# Revit family: CCIRC Emergency Circular Lighting_Non-Hosted_R19
name_source: partatom
category: Lighting Fixtures
units: mm (PartAtom-declared; Revit-internal decimal feet)

## family parameters
Always vertical = Yes
Cut with Voids When Loaded = No
Light Source = Yes
OmniClass Number = 23.80.70.00
OmniClass Title = Lighting
Part Type = Normal
Room Calculation Point = No
Round Connector Dimension = Use Diameter
Shared = No
Work Plane-Based = No

## types (7) — shared parameters
Applicable Standards = BS EN 60598.2.22, BS 5266
Battery Type = Lithium Iron Phosphate (LiFePO4)
Charging Method = Intelligent Current Limited Constant Voltage
Color Filter = 16777215
Construction = Polycarbonate
Diffuser = Polycarbonate Diffuser
Dimensions (L x W x H) = 327mm (Diameter) x 100mm (Height)
Dimming Lamp Color Temperature Shift = <None>
Emit Shape Visible in Rendering = No
IP Rating = IP54
Lamp = LED module, 4,000K natural white, 50,000h life, Ra>80
Manufacturer = Clevertronics
Mounting = Surface Mount
Operating Mode = Sustained
Operating Temperature = 1˚C to 40˚C
Photometric Web File = 6002_CCIRC-HV(S4)_EM220mA_23082021-02_IES2002.IES
Tilt Angle = 90.00°
Weight = 1.8 kg
zero-valued in all types: Default Elevation

## per-type parameters (varying)
| type | AS2293 Classification | Description | MIC Number | Operating Voltage | Power Consumption (Lamp ON Max Charge) | Power Consumption (Lamp ON Standby Charge) | Power Consumption (Lamp Off Standby) | Power Factor | Replacement Battery | Replacement Driver | Replacement Emergency Driver | Replacement Item | Replacement lamp | Sensor | Testing System | Total Lumen Output | Type Comments |
| CCIRC-ZW |  | CLP Premium Circular LED Emergency Luminaire, Trim colour white | UKC02110010001 | 220-240V AC; 50Hz | 16.5 Watts | 13W | 1.3W |  | 1550230 BATT:LP 3.2V 6400mAh.200mm lead.Brkt. | 1330091 LED Driver - 20w Stallion, 380mA | UKM02170190001 CLIFE-CKIT-ZW-IC1-650, Lifelight, Control Only, LP, ZW, 650mA, No Plug | 8001450 PCA:Powerline Node ZW, #CT10310-A6 | 8002801 PCA: CLE 220mm 2500lm 840 ADV4 EM SO |  | Zoneworks computerised testing | 1300lm @104lm/W |  |
| CCIRC | C0=D40 C90=D40 | LP Premium Circular LED Emergency Luminaire, Trim colour white, 
Enabled with Clevertest Plus
LP Premium Circular LED Emergency Luminaire, Trim colour white, 
Enabled with Clevertest Plus
LP Premium Circular LED Emergency Luminaire, Trim colour White, Enabled with Clevertest Plus | AUC02310010001 | 220-240V AC; 50Hz | 15 W | 13 W | 1.0 W | 0.93 | 1550010 | 1330091 | AUM02370470001
CLIFE-CKIT-NP-220
AUM02370470001
CLIFE-CKIT-NP-220
AUM02370470001
CLIFE-CKIT-NP-220
AUM02370470001
CLIFE-CKIT-NP-220
AUM02370470001 - CLIFE-CKIT-NP-220 |  | 8002801 |  | Clevertest Plus Enabled (Not activated by default) | 1300lm @104lm/W |  |
| CCIRC-HV | C0=D40 C90=D40 | LP Premium Circular LED Emergency Luminaire, Trim colour white | AUC02810020001 | 220-240V AC; 50Hz | 16 W | 13 W | 1.3 W | 0.93 | 1550010 | 1330091 | AUM02870500001 CLIFE-CKIT-HV-NP-220 | 8003191 | 8011800 |  | Zoneworks XT HIVE (RF) | 1460lm @118lm/W | Circular, LED, LP, Hive |
| CCIRC-MS-HL | C0=D25 C90=D25 | LP Premium Circular LED Emergency Luminaire with Microwave Sensor Control 
of the Lamps (Hi/Lo function), Trim colour white, Enabled with Clevertest Plus
LP Premium Circular LED Emergency Luminaire with Microwave Sensor Control 
of the Lamps (Hi/Lo function), Trim colour white, Enabled with Clevertest Plus
LP Premium Circular LED Emergency Luminaire with Microwave Sensor Control 
of the Lamps (Hi/Lo function), Trim colour white, Enabled with Clevertest Plus
LP Premium Circular LED Emergency Luminaire with Microwave Sensor Control 
of the Lamps (Hi/Lo function), Trim colour white, Enabled with Clevertest Plus
LP Premium Circular LED Emergency Luminaire with Microwave Sensor Control 
of the Lamps (Hi/Lo function), Trim colour white, Enabled with Clevertest Plus
LP Premium Circular LED Emergency Luminaire with Microwave Sensor Control 
of the Lamps (Hi/Lo function), Trim colour white, Enabled with Clevertest Plus
LP Premium Circular LED Emergency Luminaire with Microwave Sensor Control 
of the Lamps (Hi/Lo function), Trim colour white, Enabled with Clevertest Plus
LP Premium Circular LED Emergency Luminaire with Microwave Sensor Control 
of the Lamps (Hi/Lo function), Trim colour white, Enabled with Clevertest Plus
LP Premium Circular LED Emergency Luminaire with Microwave Sensor Control 
of the Lamps (Hi/Lo function), Trim colour white, Enabled with Clevertest Plus
LP Premium Circular LED Emergency Luminaire with Microwave Sensor Control of the Lamps (Hi/Lo function), Trim colour white, Enabled with Clevertest Plus | AUC02310020001 | 220-240V AC; 50Hz | 18 W | 7 W | 1.0 W | 0.95 | 1550010 | 1330037 | AUM02370170001 CLIFE-CKIT-NP |  | 8002801 | 1190310 | Clevertest Plus Enabled (Not activated by default) | 1300lm @104lm/W | Circular, LED, MS, HL, LP, OWC, CTP |
| CCIRC-MS-HL-HV | C0=D25 C90=D25 | LP Premium Circular LED Emergency Luminaire with Microwave Sensor Control 
of the Lamps (Hi/Lo function), Trim colour white
LP Premium Circular LED Emergency Luminaire with Microwave Sensor Control of the Lamps (Hi/Lo function), Trim colour white | AUC02810040001 | 220-240V AC; 50Hz | 18 W | 7.3 W | 1.3 W | 0.95 | 1550010 | 1330037 | AUM02870160001 CLIFE-CKIT-HV-NP | 8003189 | 8002801 |  | Zoneworks XT HIVE (RF) | 1300lm @104lm/W | Circular, LED, MS, HL, LP, HV |
| CCIRC-DD-ZW | C0=D25 C90=D25 | LP Premium Circular LED Emergency Luminaire with Dali Driver, Trim colour white | AUC02110010001 | 220-240V AC; 50Hz | 16 W | 13 W | 1.3 W | 0.95 | 1550010 | 1330041 | AUM02170100001 CLIFE-CKIT-ZW-NP | 8001450 | 8002801 |  | Zoneworks computerized testing | 1300lm @104lm/W |  |
| CCIRC-DD-HV | C0=D25 C90=D25 | LP Premium Circular LED Emergency Luminaire with Dali Driver, Trim colour white | AUC02810030001 | 240V AC; 50Hz | 16 W | 13 W | 1.3 W | 0.95 | 1550010 | 1330041 | AUM02870160001 CLIFE-CKIT-HV-NP | 8003190 | 8002801 |  | Zoneworks computerized testing | 1300lm @104lm/W | Circular, LED, LP, Dali Driver, Hive |

note: column(s) folded — value = type name in every type: Model

## geometry (parser evidence)
native form markers: Sweep x3
no freeform markers — native parametric forms only
